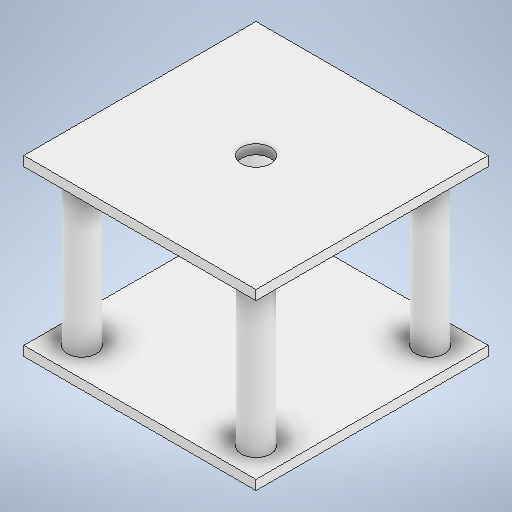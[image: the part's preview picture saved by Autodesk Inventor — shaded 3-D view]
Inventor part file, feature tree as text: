
AUTODESK INVENTOR PART (.ipt)
format: ipt  version: 2025.3 (Build 293356000, 356)  size: 230,912 bytes
history: native  units: mm
features: extrude x4, sketch x4, other x1
ambient origin geometry x8: Origin, YZ Plane, XZ Plane, XY Plane, X Axis, Y Axis, Z Axis, Center Point
bodies: Body1 (feature_tree)
feature tree (9):
  other  "Sólido1"
  extrude  "Extrusión1"  Depth=120.0mm
  extrude  "Extrusión2"  Depth=90.0mm
  extrude  "Extrusión3"  Depth=90.0mm
  extrude  "Extrusión4"  Depth=10.0mm
  sketch  "Boceto1"  dims[d0=120.0mm d1=120.0mm]
  sketch  "Boceto2"  dims[d2=5.0mm d3=0.0mm d4=90.0mm]
  sketch  "Boceto3"  dims[d5=90.0mm d6=15.0mm]
  sketch  "Boceto4"  dims[d7=15.0mm d8=15.0mm d9=15.0mm d10=80.0mm d11=0.0mm d12=120.0mm d13=120.0mm d14=5.0mm d15=0.0mm d16=15.0mm d17=10.0mm d18=0.0mm d19=0.5mm d20=0.872665mm]
